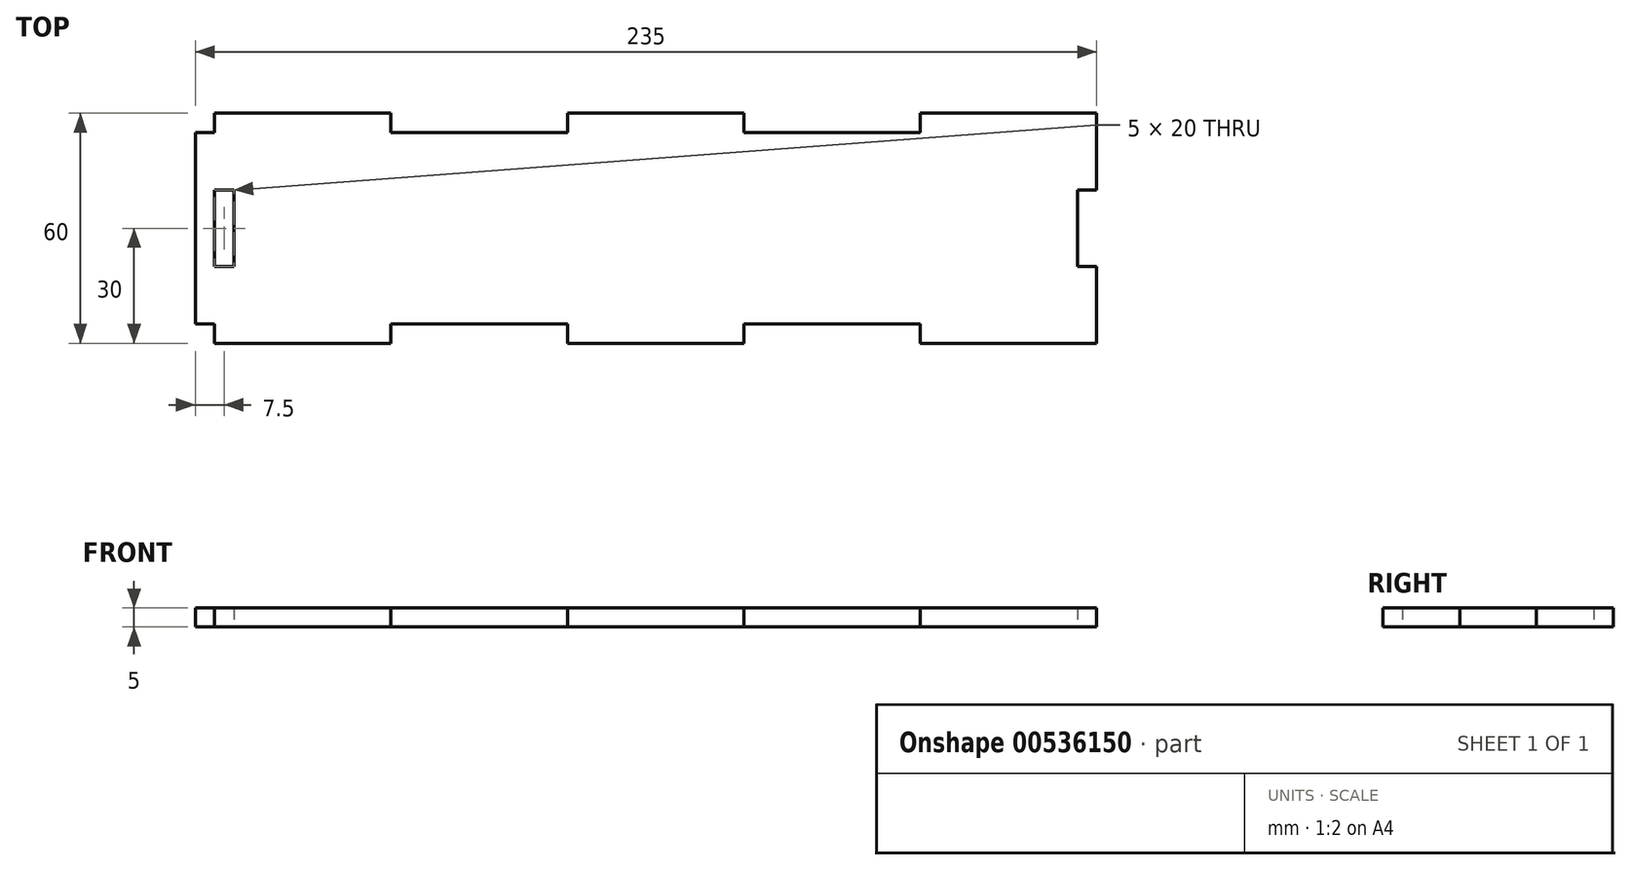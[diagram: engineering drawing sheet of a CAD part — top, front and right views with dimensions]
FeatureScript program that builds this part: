
annotation { "Feature Type Name" : "Feature", "Feature Type Description" : "" }
export const myFeature = defineFeature(function(context is Context, id is Id, definition is map)
    precondition{}
    {
        {
            var Q0;
            Q0=qCreatedBy(makeId("Top.planeOp"),FACE);
            var sketch = newSketch(context, id + "F0", { "sketchPlane" : qUnion([Q0])});
            skLineSegment(sketch, "E0.bottom", {"start": v(69, 25) * mm, "end": v(23, 25) * mm});
            skLineSegment(sketch, "E0.top", {"start": v(69, -25) * mm, "end": v(23, -25) * mm});
            skLineSegment(sketch, "E0.left", {"start": v(110, 10) * mm, "end": v(110, -10) * mm});
            skLineSegment(sketch, "E0.right", {"start": v(-110, 10) * mm, "end": v(-110, -10) * mm});
            skPoint(sketch, "E0.middle", {"position": v(0, 0) * mm});
            skLineSegment(sketch, "E1.bottom", {"start": v(115, 30) * mm, "end": v(-115, 30) * mm, "construction": true});
            skLineSegment(sketch, "E1.top", {"start": v(115, -30) * mm, "end": v(-115, -30) * mm, "construction": true});
            skLineSegment(sketch, "E1.left", {"start": v(115, 30) * mm, "end": v(115, -30) * mm, "construction": true});
            skLineSegment(sketch, "E1.right", {"start": v(-115, 10) * mm, "end": v(-115, -10) * mm, "construction": true});
            skLineSegment(sketch, "E2", {"start": v(-110, 10) * mm, "end": v(-115, 10) * mm});
            skLineSegment(sketch, "E3", {"start": v(-115, 30) * mm, "end": v(-69, 30) * mm});
            skLineSegment(sketch, "E4", {"start": v(-69, 30) * mm, "end": v(-69, 25) * mm});
            skLineSegment(sketch, "E5", {"start": v(-23, 25) * mm, "end": v(-23, 30) * mm});
            skLineSegment(sketch, "E6", {"start": v(-23, 30) * mm, "end": v(23, 30) * mm});
            skLineSegment(sketch, "E7", {"start": v(23, 30) * mm, "end": v(23, 25) * mm});
            skLineSegment(sketch, "E8", {"start": v(69, 25) * mm, "end": v(69, 30) * mm});
            skLineSegment(sketch, "E9", {"start": v(69, 30) * mm, "end": v(115, 30) * mm});
            skLineSegment(sketch, "E10", {"start": v(115, 30) * mm, "end": v(115, 10) * mm});
            skLineSegment(sketch, "E11", {"start": v(115, 10) * mm, "end": v(110, 10) * mm});
            skLineSegment(sketch, "E12.MirrorCS", {"start": v(-110, -10) * mm, "end": v(-115, -10) * mm});
            skLineSegment(sketch, "E13.MirrorCS", {"start": v(-69, -30) * mm, "end": v(-69, -25) * mm});
            skLineSegment(sketch, "E14.MirrorCS", {"start": v(-23, -25) * mm, "end": v(-23, -30) * mm});
            skLineSegment(sketch, "E15.MirrorCS", {"start": v(23, -30) * mm, "end": v(23, -25) * mm});
            skLineSegment(sketch, "E16.MirrorCS", {"start": v(69, -25) * mm, "end": v(69, -30) * mm});
            skLineSegment(sketch, "E17.MirrorCS", {"start": v(115, -10) * mm, "end": v(110, -10) * mm});
            skLineSegment(sketch, "E18", {"start": v(-115, -30) * mm, "end": v(-69, -30) * mm});
            skLineSegment(sketch, "E19", {"start": v(-23, -30) * mm, "end": v(23, -30) * mm});
            skLineSegment(sketch, "E20", {"start": v(69, -30) * mm, "end": v(115, -30) * mm});
            skLineSegment(sketch, "E21", {"start": v(115, -30) * mm, "end": v(115, -10) * mm});
            skPoint(sketch, "E22.orphan", {"position": v(-110, -25) * mm});
            skLineSegment(sketch, "E23.trimOffspring", {"start": v(-23, -25) * mm, "end": v(-69, -25) * mm});
            skPoint(sketch, "E24.orphan", {"position": v(110, -25) * mm});
            skPoint(sketch, "E25.orphan", {"position": v(110, 25) * mm});
            skLineSegment(sketch, "E26.trimOffspring", {"start": v(-23, 25) * mm, "end": v(-69, 25) * mm});
            skPoint(sketch, "E27.orphan", {"position": v(-110, 25) * mm});
            skLineSegment(sketch, "E28", {"start": v(-115, 10) * mm, "end": v(-115, -10) * mm});
            skLineSegment(sketch, "E29", {"start": v(-120, -25) * mm, "end": v(-120, 25) * mm});
            skLineSegment(sketch, "E30", {"start": v(-115, -30) * mm, "end": v(-115, -25) * mm});
            skLineSegment(sketch, "E31", {"start": v(-115, -25) * mm, "end": v(-120, -25) * mm});
            skLineSegment(sketch, "E32", {"start": v(-115, 30) * mm, "end": v(-115, 25) * mm});
            skLineSegment(sketch, "E33", {"start": v(-115, 25) * mm, "end": v(-120, 25) * mm});
            skPoint(sketch, "E34.orphan", {"position": v(-120, 30) * mm});
            skSolve(sketch);
        }
        {
            var Q0;
            Q0 = qSketchRegion(id + "F0", true);
            extrude(context, id + "F1", {"entities" : qUnion([Q0]), "depth" : 5 * mm, "offsetDistance" : 25 * mm});
        }
    });
